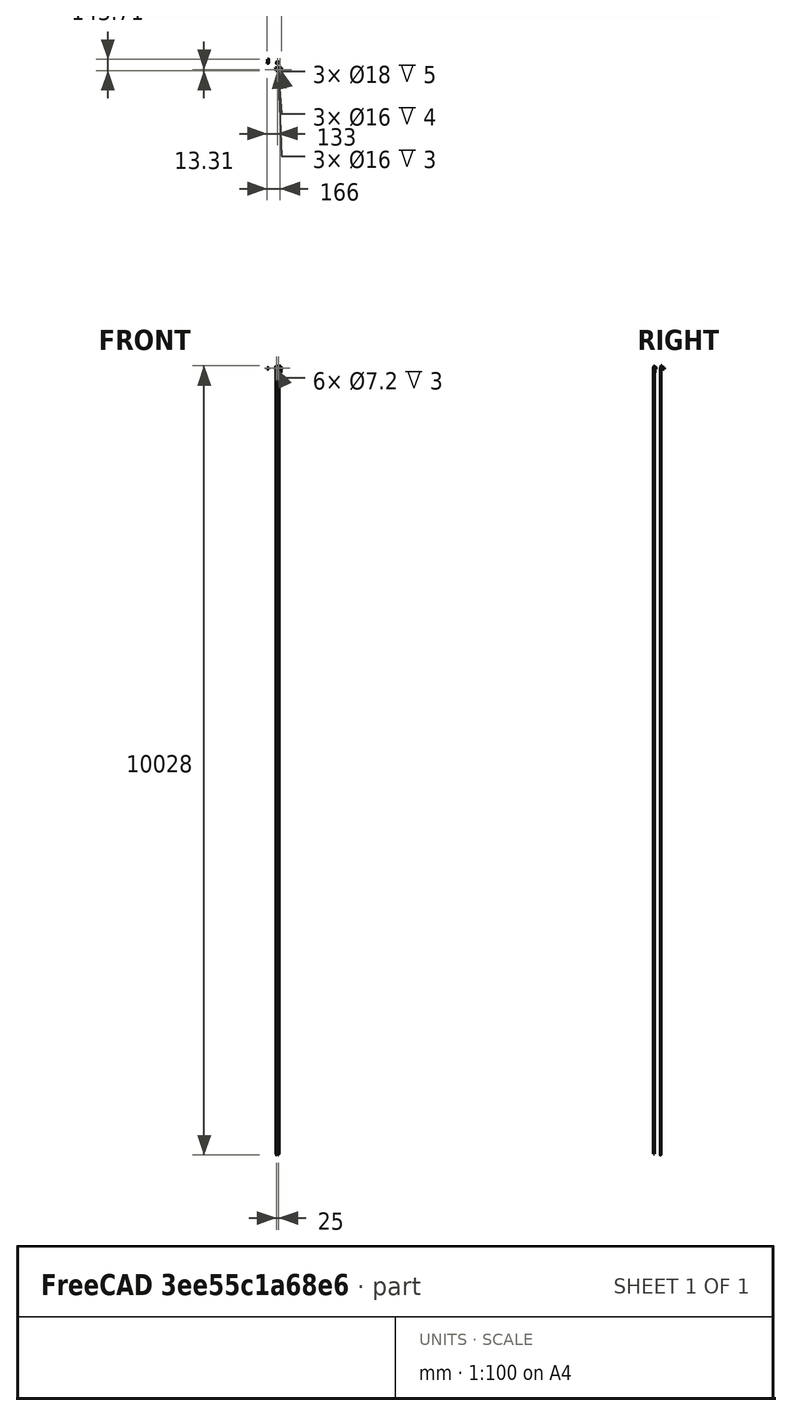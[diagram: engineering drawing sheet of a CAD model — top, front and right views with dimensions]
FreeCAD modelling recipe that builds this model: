
FCSTD DOCUMENT  (FreeCAD 0.15R4671 (Git))
Label: XCarrage_Hotend_AluRepRap_3DA-002
License: All rights reserved
LicenseURL: http://en.wikipedia.org/wiki/All_rights_reserved
objects: Sketcher::SketchObject×18, PartDesign::Pocket×15, PartDesign::Fillet×10, Mesh::Feature×5, Part::Feature×5, PartDesign::Pad×3, PartDesign::Chamfer×1
note: 70 computed .brp shape members not serialized (recipe doc carries the construction recipe); baked Part::Feature solids carry a one-line shape summary decoded from their .brp

FEATURE [Sketcher::SketchObject] Sketch
  Placement = pos=(0,-58,0) rot=(1,0,0;1.5708rad)
  sketch-geometry (4):
    g0: LineSegment StartX=93 StartY=-10 StartZ=0 EndX=149 EndY=-10 EndZ=0
    g1: LineSegment StartX=149 StartY=-10 StartZ=0 EndX=149 EndY=18 EndZ=0
    g2: LineSegment StartX=149 StartY=18 StartZ=0 EndX=93 EndY=18 EndZ=0
    g3: LineSegment StartX=93 StartY=18 StartZ=0 EndX=93 EndY=-10 EndZ=0
  constraints (8):
    c: Coincident(g0,g1)
    c: Coincident(g1,g2)
    c: Coincident(g2,g3)
    c: Coincident(g3,g0)
    c: Horizontal(g0)
    c: Horizontal(g2)
    c: Vertical(g1)
    c: Vertical(g3)
FEATURE [PartDesign::Pad] Pad
  Length = 5
  Length2 = 100
  Placement = pos=(0,-58,0) rot=(1,0,0;1.5708rad)
  Sketch = -> Sketch
  Type = 0
FEATURE [Mesh::Feature] HexHotEnd  label="HexHotEnd1"
  Placement = pos=(122,-78,-20) rot=(0,0,1;0rad)
FEATURE [Mesh::Feature] PNEUMATIC_NIPPLE
  Placement = pos=(111,-50,-28) rot=(0,-1,0;1.5708rad)
FEATURE [Part::Feature] Part__Feature  label="LJ18A3"
  Placement = pos=(155,-78,-52) rot=(0,0,1;0rad)
  shape: bbox 17.85 x 17.85 x 79.1 mm, 11 faces (baked)
FEATURE [Mesh::Feature] Hotend_Dummy___GTMax3D  label="Hotend_Dummy_-_GTMax3D"
  Placement = pos=(173,-78,-48.4) rot=(0,0,1;0rad)
FEATURE [Part::Feature] Part__Feature001  label="JHead_Nozzle"
  shape: bbox 17.41 x 24.4 x 17.41 mm, 34 faces (baked)
FEATURE [Part::Feature] Part__Feature002  label="JHead_Nozzle001"
  shape: bbox 16 x 40 x 16 mm, 230 faces (baked)
FEATURE [Sketcher::SketchObject] Sketch002
  Placement = pos=(0,-63,0) rot=(1,0,0;1.5708rad)
  Support = -> Pad [Face6]
  sketch-geometry (4):
    g0: LineSegment StartX=104 StartY=18 StartZ=0 EndX=138 EndY=18 EndZ=0
    g1: LineSegment StartX=138 StartY=18 StartZ=0 EndX=138 EndY=6 EndZ=0
    g2: LineSegment StartX=138 StartY=6 StartZ=0 EndX=104 EndY=6 EndZ=0
    g3: LineSegment StartX=104 StartY=6 StartZ=0 EndX=104 EndY=18 EndZ=0
  constraints (9):
    c: Coincident(g0,g1)
    c: Coincident(g1,g2)
    c: Coincident(g2,g3)
    c: Coincident(g3,g0)
    c: Horizontal(g0)
    c: Horizontal(g2)
    c: Vertical(g1)
    c: Vertical(g3)
    c: DistanceY(g2,g0) = 12
FEATURE [PartDesign::Pad] Pad001
  Length = 28
  Length2 = 100
  Placement = pos=(0,-58,0) rot=(1,0,0;1.5708rad)
  Sketch = -> Sketch002
  Type = 0
FEATURE [Sketcher::SketchObject] Sketch003
  Placement = pos=(0,-58,18) rot=(0,0,1;3.14159rad)
  Support = -> Pad001 [Face10]
  sketch-geometry (1):
    g0: Circle CenterX=-122 CenterY=20 CenterZ=0 NormalX=0 NormalY=0 NormalZ=1 Radius=8
  constraints (1):
    c: Radius(g0) = 8
FEATURE [PartDesign::Pocket] Pocket
  Length = 4
  Placement = pos=(0,-58,0) rot=(1,0,0;1.5708rad)
  Sketch = -> Sketch003
  Type = 0
FEATURE [Sketcher::SketchObject] Sketch004
  Placement = pos=(0,-58,14) rot=(0,0,1;3.14159rad)
  Support = -> Pocket [Face12]
  sketch-geometry (1):
    g0: Circle CenterX=-122 CenterY=20 CenterZ=0 NormalX=0 NormalY=0 NormalZ=1 Radius=6
  constraints (1):
    c: Radius(g0) = 6
FEATURE [PartDesign::Pocket] Pocket001
  Length = 5
  Placement = pos=(0,-58,0) rot=(1,0,0;1.5708rad)
  Sketch = -> Sketch004
  Type = 0
FEATURE [Sketcher::SketchObject] Sketch005
  Placement = pos=(0,-58,6) rot=(1,0,0;3.14159rad)
  Support = -> Pocket001 [Face8]
  sketch-geometry (1):
    g0: Circle CenterX=122 CenterY=20 CenterZ=0 NormalX=0 NormalY=0 NormalZ=1 Radius=8
  constraints (1):
    c: Radius(g0) = 8
FEATURE [PartDesign::Pocket] Pocket002
  Length = 3
  Placement = pos=(0,-58,0) rot=(1,0,0;1.5708rad)
  Sketch = -> Sketch005
  Type = 0
FEATURE [Sketcher::SketchObject] Sketch006
  Placement = pos=(0,-58,0) rot=(-1,0,0;1.5708rad)
  Support = -> Pocket002 [Face4]
  sketch-geometry (4):
    g0: LineSegment StartX=142 StartY=10 StartZ=0 EndX=168 EndY=10 EndZ=0
    g1: LineSegment StartX=168 StartY=10 StartZ=0 EndX=168 EndY=5 EndZ=0
    g2: LineSegment StartX=168 StartY=5 StartZ=0 EndX=142 EndY=5 EndZ=0
    g3: LineSegment StartX=142 StartY=5 StartZ=0 EndX=142 EndY=10 EndZ=0
  constraints (8):
    c: Coincident(g0,g1)
    c: Coincident(g1,g2)
    c: Coincident(g2,g3)
    c: Coincident(g3,g0)
    c: Horizontal(g0)
    c: Horizontal(g2)
    c: Vertical(g1)
    c: Vertical(g3)
FEATURE [PartDesign::Pad] Pad002
  Length = 33
  Length2 = 100
  Placement = pos=(0,-58,0) rot=(1,0,0;1.5708rad)
  Reversed = true
  Sketch = -> Sketch006
  Type = 0
FEATURE [PartDesign::Chamfer] Chamfer
  Base = -> Pad002 [Edge21]
  Placement = pos=(0,-58,0) rot=(1,0,0;1.5708rad)
  Size = 18.99
FEATURE [PartDesign::Fillet] Fillet
  Base = -> Chamfer [Edge34,Edge46]
  Placement = pos=(0,-58,0) rot=(1,0,0;1.5708rad)
  Radius = 12.99
FEATURE [PartDesign::Fillet] Fillet001
  Base = -> Fillet [Edge32]
  Placement = pos=(0,-58,0) rot=(1,0,0;1.5708rad)
  Radius = 10
FEATURE [PartDesign::Fillet] Fillet002
  Base = -> Fillet001 [Edge25,Edge22]
  Placement = pos=(0,-58,0) rot=(1,0,0;1.5708rad)
  Radius = 4
FEATURE [Sketcher::SketchObject] Sketch007
  Placement = pos=(0,-58,-5) rot=(0,0,1;3.14159rad)
  Support = -> Fillet002 [Face8]
  sketch-geometry (1):
    g0: Circle CenterX=-155 CenterY=20 CenterZ=0 NormalX=0 NormalY=0 NormalZ=1 Radius=9
  constraints (1):
    c: Radius(g0) = 9
FEATURE [PartDesign::Pocket] Pocket003
  Length = 5
  Placement = pos=(0,-58,0) rot=(1,0,0;1.5708rad)
  Sketch = -> Sketch007
  Type = 0
FEATURE [PartDesign::Fillet] Fillet003
  Base = -> Pocket003 [Edge13]
  Placement = pos=(0,-58,0) rot=(1,0,0;1.5708rad)
  Radius = 2
FEATURE [PartDesign::Fillet] Fillet004
  Base = -> Fillet003 [Edge25,Edge32]
  Placement = pos=(0,-58,0) rot=(1,0,0;1.5708rad)
  Radius = 2
FEATURE [Sketcher::SketchObject] Sketch008
  Placement = pos=(0,-63,0) rot=(1,0,0;1.5708rad)
  Support = -> Fillet004 [Face1]
  sketch-geometry (2):
    g0: Circle CenterX=107 CenterY=1 CenterZ=0 NormalX=0 NormalY=0 NormalZ=1 Radius=1.8
    g1: Circle CenterX=132 CenterY=1 CenterZ=0 NormalX=0 NormalY=0 NormalZ=1 Radius=1.8
  constraints (5):
    c: DistanceX(g0,g1) = 25
    c: DistanceX(g0) = 107
    c: DistanceY(g0) = 1
    c: Radius(g0) = 1.8
    c: Equal(g0,g1)
FEATURE [PartDesign::Pocket] Pocket004
  Length = 5
  Placement = pos=(0,-58,0) rot=(1,0,0;1.5708rad)
  Sketch = -> Sketch008
  Type = 1
FEATURE [Sketcher::SketchObject] Sketch009
  Placement = pos=(0,-63,0) rot=(1,0,0;1.5708rad)
  Support = -> Pocket004 [Face1]
  sketch-geometry (2):
    g0: Circle CenterX=107 CenterY=1 CenterZ=0 NormalX=0 NormalY=0 NormalZ=1 Radius=3.6
    g1: Circle CenterX=132 CenterY=1 CenterZ=0 NormalX=0 NormalY=0 NormalZ=1 Radius=3.6
  constraints (2):
    c: Radius(g1) = 3.6
    c: Equal(g1,g0)
FEATURE [PartDesign::Pocket] Pocket005
  Length = 3
  Placement = pos=(0,-58,0) rot=(1,0,0;1.5708rad)
  Sketch = -> Sketch009
  Type = 0
FEATURE [Mesh::Feature] HexNutStyle1_M  label="HexNutStyle1_M3"
  Placement = pos=(123,43,34) rot=(1,0,0;1.5708rad)
FEATURE [Mesh::Feature] HexNutStyle1_M001  label="HexNutStyle1_M004"
  Placement = pos=(148,43,34) rot=(1,0,0;1.5708rad)
FEATURE [Sketcher::SketchObject] Sketch010
  Placement = pos=(0,-91,0) rot=(1,0,0;1.5708rad)
  Support = -> Pocket005 [Face19]
  sketch-geometry (2):
    g0: Circle CenterX=108.75 CenterY=12 CenterZ=0 NormalX=0 NormalY=0 NormalZ=1 Radius=1.8
    g1: Circle CenterX=133.75 CenterY=12 CenterZ=0 NormalX=0 NormalY=0 NormalZ=1 Radius=1.8
  constraints (2):
    c: Radius(g0) = 1.8
    c: Equal(g0,g1)
FEATURE [PartDesign::Pocket] Pocket006
  Length = 21
  Placement = pos=(0,-58,0) rot=(1,0,0;1.5708rad)
  Sketch = -> Sketch010
  Type = 0
FEATURE [Sketcher::SketchObject] Sketch011
  Placement = pos=(0,-91,0) rot=(1,0,0;1.5708rad)
  Support = -> Pocket006 [Face19]
  sketch-geometry (2):
    g0: Circle CenterX=133.75 CenterY=12 CenterZ=0 NormalX=0 NormalY=0 NormalZ=1 Radius=3.5
    g1: Circle CenterX=108.75 CenterY=12 CenterZ=0 NormalX=0 NormalY=0 NormalZ=1 Radius=3.5
  constraints (2):
    c: Radius(g0) = 3.5
    c: Equal(g0,g1)
FEATURE [PartDesign::Pocket] Pocket007
  Length = 11
  Placement = pos=(0,-58,0) rot=(1,0,0;1.5708rad)
  Sketch = -> Sketch011
  Type = 0
FEATURE [Sketcher::SketchObject] Sketch012
  Placement = pos=(0,-58,18) rot=(0,0,1;3.14159rad)
  Support = -> Pocket007 [Face5]
  sketch-geometry (6):
    g0: LineSegment StartX=-140 StartY=29 StartZ=0 EndX=-129 EndY=29 EndZ=0
    g1: LineSegment StartX=-115 StartY=29 StartZ=0 EndX=-102 EndY=29 EndZ=0
    g2: ArcOfCircle CenterX=-122 CenterY=20 CenterZ=0 NormalX=0 NormalY=0 NormalZ=1 Radius=11.4018 StartAngle=0.909753 EndAngle=2.23184
    g3: LineSegment StartX=-140 StartY=29 StartZ=0 EndX=-140 EndY=34 EndZ=0
    g4: LineSegment StartX=-140 StartY=34 StartZ=0 EndX=-102 EndY=34 EndZ=0
    g5: LineSegment StartX=-102 StartY=34 StartZ=0 EndX=-102 EndY=29 EndZ=0
  constraints (5):
    c: Coincident(g3,g4)
    c: Coincident(g4,g5)
    c: Coincident(g0,g2)
    c: Coincident(g1,g2)
    c: Coincident(g1,g5)
FEATURE [PartDesign::Pocket] Pocket008
  Length = 5
  Placement = pos=(0,-58,0) rot=(1,0,0;1.5708rad)
  Sketch = -> Sketch012
  Type = 1
FEATURE [PartDesign::Fillet] Fillet005
  Base = -> Pocket008 [Edge84,Edge88]
  Placement = pos=(0,-58,0) rot=(1,0,0;1.5708rad)
  Radius = 1
FEATURE [Part::Feature] Fillet006  label="XCarrage_Hotend_AluRepRap_3DA-002_x"
  shape: bbox 75 x 33 x 28 mm, 50 faces (baked)
FEATURE [Part::Feature] Part__Feature003  label="HotendRetainerClip"
  shape: bbox 34 x 11.15 x 12 mm, 25 faces (baked)
FEATURE [Sketcher::SketchObject] Sketch013
  Placement = pos=(0,0,18) rot=(0,0,1;0rad)
  Support = -> Fillet006 [Face1]
  sketch-geometry (4):
    g0: LineSegment StartX=101.75 StartY=-78 StartZ=0 EndX=141 EndY=-78 EndZ=0
    g1: LineSegment StartX=141 StartY=-78 StartZ=0 EndX=141 EndY=-91.3096 EndZ=0
    g2: LineSegment StartX=141 StartY=-91.3096 StartZ=0 EndX=101.75 EndY=-91.3096 EndZ=0
    g3: LineSegment StartX=101.75 StartY=-91.3096 StartZ=0 EndX=101.75 EndY=-78 EndZ=0
  constraints (8):
    c: Coincident(g0,g1)
    c: Coincident(g1,g2)
    c: Coincident(g2,g3)
    c: Coincident(g3,g0)
    c: Horizontal(g0)
    c: Horizontal(g2)
    c: Vertical(g1)
    c: Vertical(g3)
FEATURE [PartDesign::Pocket] Pocket009  label="XCarrage_Hotend_AluRepRap_3DA-002_y"
  Length = 5
  Sketch = -> Sketch013
  Type = 1
FEATURE [Sketcher::SketchObject] Sketch014
  Placement = pos=(0,0,6) rot=(1,0,0;3.14159rad)
  Support = -> Pocket009 [Face13]
  sketch-geometry (8):
    g0: LineSegment StartX=105.75 StartY=76 StartZ=0 EndX=111.75 EndY=76 EndZ=0
    g1: LineSegment StartX=111.75 StartY=76 StartZ=0 EndX=111.75 EndY=73.25 EndZ=0
    g2: LineSegment StartX=111.75 StartY=73.25 StartZ=0 EndX=105.75 EndY=73.25 EndZ=0
    g3: LineSegment StartX=105.75 StartY=73.25 StartZ=0 EndX=105.75 EndY=76 EndZ=0
    g4: LineSegment StartX=130.75 StartY=76 StartZ=0 EndX=136.75 EndY=76 EndZ=0
    g5: LineSegment StartX=136.75 StartY=76 StartZ=0 EndX=136.75 EndY=73.25 EndZ=0
    g6: LineSegment StartX=136.75 StartY=73.25 StartZ=0 EndX=130.75 EndY=73.25 EndZ=0
    g7: LineSegment StartX=130.75 StartY=73.25 StartZ=0 EndX=130.75 EndY=76 EndZ=0
  constraints (16):
    c: Coincident(g0,g1)
    c: Coincident(g1,g2)
    c: Coincident(g2,g3)
    c: Coincident(g3,g0)
    c: Horizontal(g0)
    c: Horizontal(g2)
    c: Vertical(g1)
    c: Vertical(g3)
    c: Coincident(g4,g5)
    c: Coincident(g5,g6)
    c: Coincident(g6,g7)
    c: Coincident(g7,g4)
    c: Horizontal(g4)
    c: Horizontal(g6)
    c: Vertical(g5)
    c: Vertical(g7)
FEATURE [PartDesign::Pocket] Pocket010  label="XCarrage_Hotend_AluRepRap_3DA-002_z"
  Length = 9.5
  Sketch = -> Sketch014
  Type = 0
FEATURE [Sketcher::SketchObject] Sketch015
  Placement = pos=(0,0,18) rot=(0,0,1;0rad)
  Support = -> Pocket010 [Face1]
  sketch-geometry (1):
    g0: Circle CenterX=122 CenterY=-78 CenterZ=0 NormalX=0 NormalY=0 NormalZ=1 Radius=8.2
  constraints (1):
    c: Radius(g0) = 8.2
FEATURE [PartDesign::Pocket] Pocket011
  Length = 4.2
  Sketch = -> Sketch015
  Type = 0
FEATURE [Sketcher::SketchObject] Sketch016
  Placement = pos=(0,0,6) rot=(1,0,0;3.14159rad)
  Support = -> Pocket011 [Face13]
  sketch-geometry (1):
    g0: Circle CenterX=122 CenterY=78 CenterZ=0 NormalX=0 NormalY=0 NormalZ=1 Radius=8.2
  constraints (1):
    c: Radius(g0) = 8.2
FEATURE [PartDesign::Pocket] Pocket012
  Length = 3.2
  Sketch = -> Sketch016
  Type = 0
FEATURE [Sketcher::SketchObject] Sketch017
  Placement = pos=(0,0,13.8) rot=(0,0,1;0rad)
  Support = -> Pocket012 [Face17]
  sketch-geometry (1):
    g0: Circle CenterX=122 CenterY=-78 CenterZ=0 NormalX=0 NormalY=0 NormalZ=1 Radius=6.2
  constraints (1):
    c: Radius(g0) = 6.2
FEATURE [PartDesign::Pocket] Pocket013
  Length = 5
  Sketch = -> Sketch017
  Type = 0
FEATURE [PartDesign::Fillet] Fillet007
  Base = -> Pocket013 [Edge79,Edge78]
  Radius = 0.5
FEATURE [PartDesign::Fillet] Fillet008
  Base = -> Fillet007 [Edge19,Edge4]
  Radius = 0.5
FEATURE [PartDesign::Fillet] Fillet009
  Base = -> Fillet008 [Edge17,Edge40]
  Radius = 0.5
FEATURE [Sketcher::SketchObject] Sketch018
  Placement = pos=(0,0,-5) rot=(0,0,1;0rad)
  Support = -> Fillet009 [Face48]
  sketch-geometry (1):
    g0: Circle CenterX=155 CenterY=-78 CenterZ=0 NormalX=0 NormalY=0 NormalZ=1 Radius=9.5
  constraints (1):
    c: Radius(g0) = 9.5
FEATURE [PartDesign::Pocket] Pocket014
  Length = 5
  Sketch = -> Sketch018
  Type = 0
FEATURE [PartDesign::Fillet] Fillet010  label="XCarrage_Hotend_AluRepRap_3DA-002"
  Base = -> Pocket014 [Edge155,Edge165]
  Radius = 0.5
